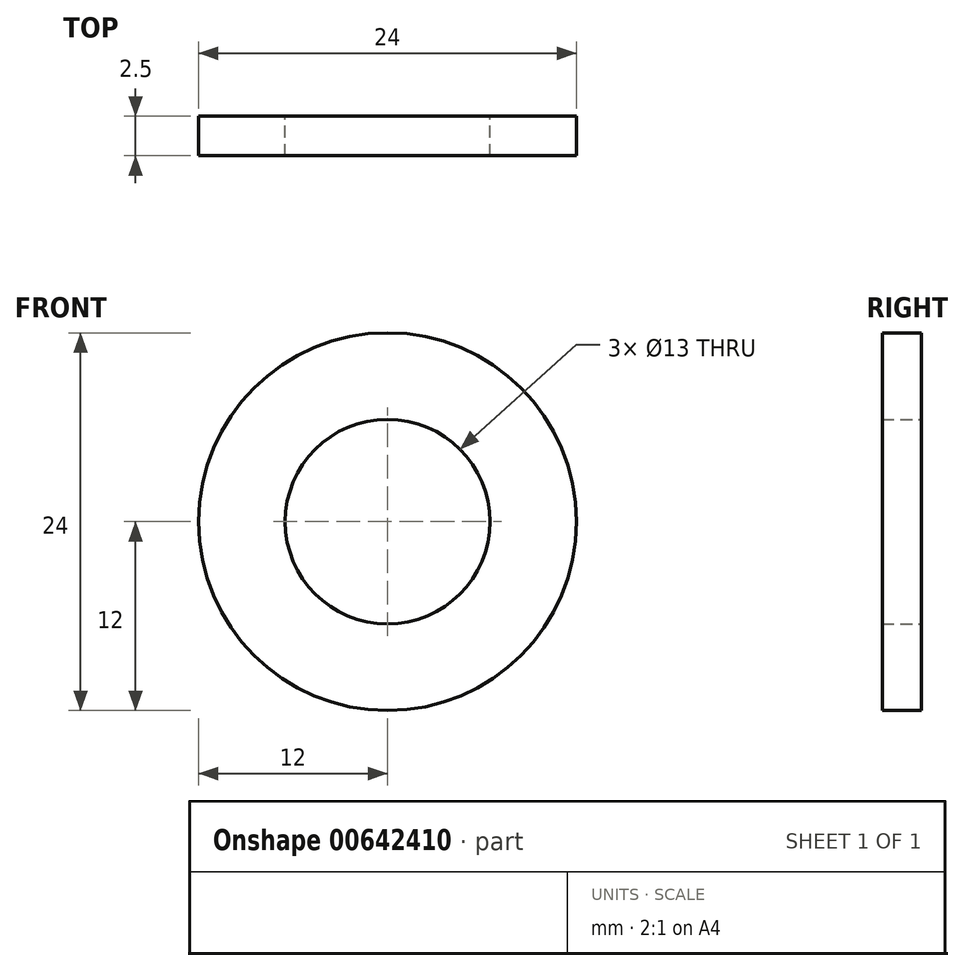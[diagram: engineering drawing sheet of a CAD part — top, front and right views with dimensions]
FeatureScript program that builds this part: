
annotation { "Feature Type Name" : "Feature", "Feature Type Description" : "" }
export const myFeature = defineFeature(function(context is Context, id is Id, definition is map)
    precondition{}
    {
        {
            var Q0;
            Q0=qCreatedBy(makeId("Front.planeOp"),FACE);
            var sketch = newSketch(context, id + "F0", { "sketchPlane" : qUnion([Q0])});
            skCircle(sketch, "E0", {"center": v(0, 0) * mm, "radius": 12 * mm});
            skCircle(sketch, "E1", {"center": v(0, 0) * mm, "radius": 6.5 * mm});
            skSolve(sketch);
        }
        {
            var Q0;
            Q0=makeQuery(id+"F0.imprint","IMPRINT",FACE,{"disambiguationData":[TD([[makeQuery(id+"F0.imprint","IMPRINT",EDGE,{"derivedFrom":sQuery(id+"F0.wireOp",EDGE,"E0")}),1.0]])]});
            extrude(context, id + "F1", {"entities" : qUnion([Q0]), "depth" : 2.5 * mm, "offsetDistance" : 25 * mm});
        }
    });
